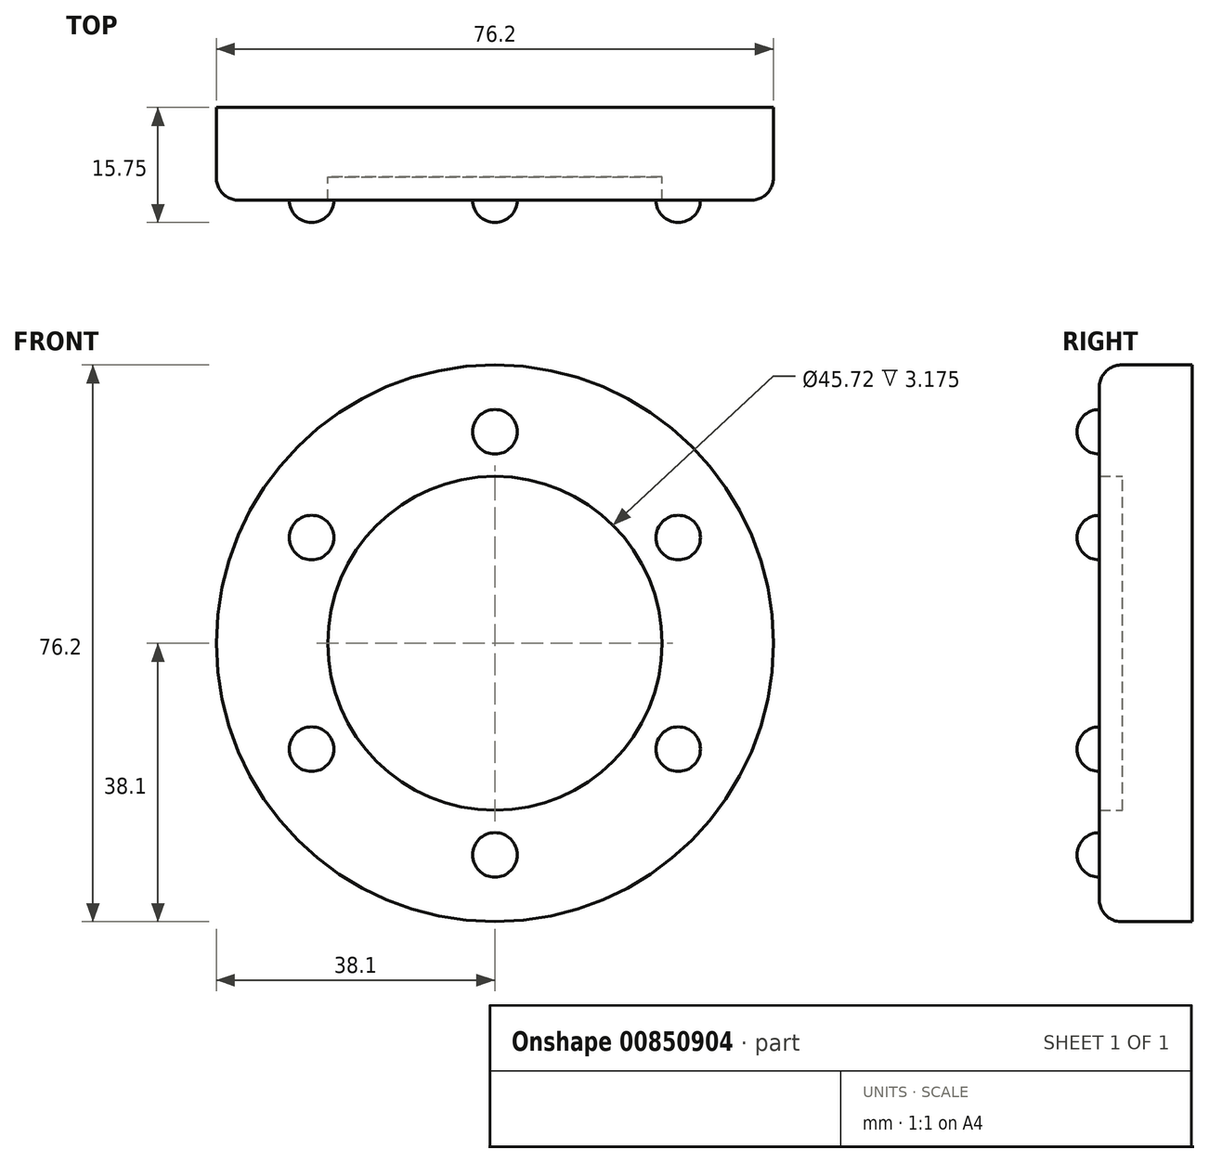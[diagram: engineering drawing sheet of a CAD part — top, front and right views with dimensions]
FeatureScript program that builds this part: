
annotation { "Feature Type Name" : "Feature", "Feature Type Description" : "" }
export const myFeature = defineFeature(function(context is Context, id is Id, definition is map)
    precondition{}
    {
        {
            var Q0;
            Q0=qCreatedBy(makeId("Front.planeOp"),FACE);
            var sketch = newSketch(context, id + "F0", { "sketchPlane" : qUnion([Q0])});
            skCircle(sketch, "E0", {"center": v(0, 0) * mm, "radius": 22.86 * mm});
            skCircle(sketch, "E1", {"center": v(0, 0) * mm, "radius": 38.1 * mm});
            skSolve(sketch);
        }
        {
            var Q0;
            Q0 = qSketchRegion(id + "F0", true);
            extrude(context, id + "F1", {"entities" : qUnion([Q0]), "depth" : 12.7 * mm, "offsetDistance" : 25.4 * mm});
        }
        {
            var Q0;
            Q0=makeQuery(id+"F1.opExtrude","CAP_EDGE",EDGE,{"disambiguationData":[OSD([sQuery(id+"F0.wireOp",EDGE,"E1")])],"isStart":false});
            fillet(context, id + "F2", {"entities" : qUnion([Q0]), "radius" : 3.05 * mm, "tangentPropagation" : true, "allowEdgeOverflow" : false});
        }
        {
            var Q0;
            Q0=makeQuery(id+"F0.imprint","IMPRINT",FACE,{"disambiguationData":[TD([[makeQuery(id+"F0.imprint","IMPRINT",EDGE,{"derivedFrom":sQuery(id+"F0.wireOp",EDGE,"E0")}),1.0]])]});
            extrude(context, id + "F3", {"entities" : qUnion([Q0]), "operationType" : NewBodyOperationType.ADD, "depth" : 9.52 * mm, "offsetDistance" : 25.4 * mm});
        }
        {
            var Q0;
            Q0=makeQuery(id+"F1.opExtrude","CAP_FACE",FACE,{"disambiguationData":[OSD([sQuery(id+"F0.wireOp",EDGE,"E0"),sQuery(id+"F0.wireOp",EDGE,"E1")])],"isStart":false});
            var sketch = newSketch(context, id + "F4", { "sketchPlane" : qUnion([Q0])});
            skLineSegment(sketch, "E2", {"start": v(0, 35.05) * mm, "end": v(0, 22.86) * mm});
            skArc(sketch, "E3", {"start": v(0, 32) * mm, "mid": v(-3.05, 28.96) * mm, "end": v(0, 25.9) * mm});
            skArc(sketch, "E4.1.0", {"start": v(-25.08, 17.53) * mm, "mid": v(-28.12, 14.48) * mm, "end": v(-25.08, 11.43) * mm});
            skArc(sketch, "E4.2.0", {"start": v(-25.08, -11.43) * mm, "mid": v(-28.12, -14.48) * mm, "end": v(-25.08, -17.53) * mm});
            skArc(sketch, "E4.3.0", {"start": v(0, -25.9) * mm, "mid": v(-3.05, -28.96) * mm, "end": v(0, -32) * mm});
            skArc(sketch, "E4.4.0", {"start": v(25.08, -11.43) * mm, "mid": v(22.03, -14.48) * mm, "end": v(25.08, -17.53) * mm});
            skArc(sketch, "E4.5.0", {"start": v(25.08, 17.53) * mm, "mid": v(22.03, 14.48) * mm, "end": v(25.08, 11.43) * mm});
            skPoint(sketch, "E4.center", {"position": v(0, 0) * mm});
            skLineSegment(sketch, "E5", {"start": v(-25.08, 56.33) * mm, "end": v(-25.08, -57.6) * mm, "construction": true});
            skLineSegment(sketch, "E6", {"start": v(0, 56.4) * mm, "end": v(0, -55.8) * mm, "construction": true});
            skLineSegment(sketch, "E7", {"start": v(25.08, 56.7) * mm, "end": v(25.08, -56.1) * mm, "construction": true});
            skLineSegment(sketch, "E8", {"start": v(-25.08, 17.53) * mm, "end": v(-25.08, 11.43) * mm});
            skLineSegment(sketch, "E9", {"start": v(-25.08, -11.43) * mm, "end": v(-25.08, -17.53) * mm});
            skLineSegment(sketch, "E10", {"start": v(0, -25.9) * mm, "end": v(0, -32) * mm});
            skLineSegment(sketch, "E11", {"start": v(25.08, 17.53) * mm, "end": v(25.08, 11.43) * mm});
            skLineSegment(sketch, "E12", {"start": v(25.08, -11.43) * mm, "end": v(25.08, -17.53) * mm});
            skSolve(sketch);
        }
        {
            var Q0;
            Q0=makeQuery(id+"F4.imprint","IMPRINT",FACE,{"disambiguationData":[TD([[makeQuery(id+"F4.imprint","IMPRINT",EDGE,{"derivedFrom":sQuery(id+"F4.wireOp",EDGE,"E4.1.0")}),1.0]])]});
            var Q1;
            Q1=makeQuery(id+"F4.imprint","IMPRINT",FACE,{"disambiguationData":[TD([[makeQuery(id+"F4.imprint","IMPRINT",EDGE,{"derivedFrom":sQuery(id+"F4.wireOp",EDGE,"E4.2.0")}),1.0]])]});
            var Q2;
            Q2=sQuery(id+"F4.wireOp",EDGE,"E5");
            revolve(context, id + "F5", {"operationType" : NewBodyOperationType.ADD, "surfaceOperationType" : NewSurfaceOperationType.NEW, "entities" : qUnion([Q0, Q1]), "axis" : qUnion([Q2]), "revolveType" : RevolveType.FULL});
        }
        {
            var Q0;
            {var subQ0=sQuery(id+"F4.wireOp",EDGE,"E3");Q0=makeQuery(id+"F4.imprint","IMPRINT",FACE,{"disambiguationData":[TD([[makeQuery(id+"F4.imprint","IMPRINT",EDGE,{"derivedFrom":subQ0}),1.0]])]});}
            var Q1;
            Q1=makeQuery(id+"F4.imprint","IMPRINT",FACE,{"disambiguationData":[TD([[makeQuery(id+"F4.imprint","IMPRINT",EDGE,{"derivedFrom":sQuery(id+"F4.wireOp",EDGE,"E4.3.0")}),1.0]])]});
            var Q2;
            Q2=sQuery(id+"F4.wireOp",EDGE,"E6");
            revolve(context, id + "F6", {"operationType" : NewBodyOperationType.ADD, "surfaceOperationType" : NewSurfaceOperationType.NEW, "entities" : qUnion([Q0, Q1]), "axis" : qUnion([Q2]), "revolveType" : RevolveType.FULL});
        }
        {
            var Q0;
            Q0=makeQuery(id+"F4.imprint","IMPRINT",FACE,{"disambiguationData":[TD([[makeQuery(id+"F4.imprint","IMPRINT",EDGE,{"derivedFrom":sQuery(id+"F4.wireOp",EDGE,"E4.5.0")}),1.0]])]});
            var Q1;
            Q1=makeQuery(id+"F4.imprint","IMPRINT",FACE,{"disambiguationData":[TD([[makeQuery(id+"F4.imprint","IMPRINT",EDGE,{"derivedFrom":sQuery(id+"F4.wireOp",EDGE,"E4.4.0")}),1.0]])]});
            var Q2;
            Q2=sQuery(id+"F4.wireOp",EDGE,"E7");
            revolve(context, id + "F7", {"operationType" : NewBodyOperationType.ADD, "surfaceOperationType" : NewSurfaceOperationType.NEW, "entities" : qUnion([Q0, Q1]), "axis" : qUnion([Q2]), "revolveType" : RevolveType.FULL});
        }
    });
